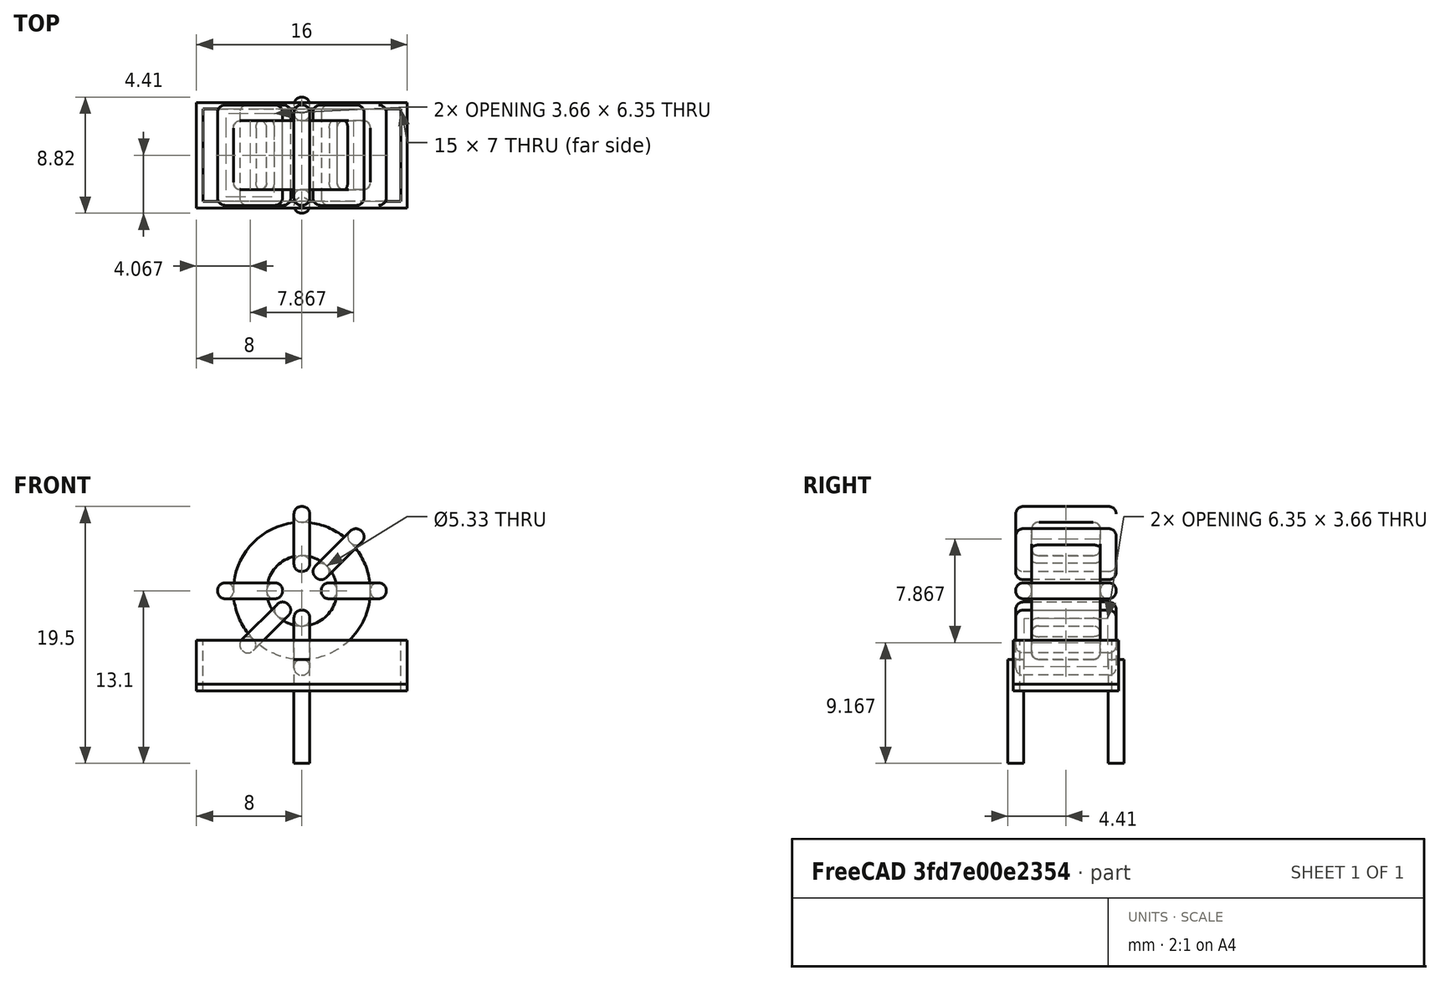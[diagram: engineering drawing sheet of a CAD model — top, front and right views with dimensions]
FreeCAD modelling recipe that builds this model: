
FCSTD DOCUMENT  (FreeCAD 0.16R6703 (Git))
Label: L_Toroid_Vertical_L16.0mm_W8.0mm_P7.62mm
License: All rights reserved
LicenseURL: http://en.wikipedia.org/wiki/All_rights_reserved
objects: Sketcher::SketchObject×8, PartDesign::Pad×8, PartDesign::Fillet×5, Spreadsheet::Sheet×1
note: 29 computed .brp shape members not serialized (recipe doc carries the construction recipe); baked Part::Feature solids carry a one-line shape summary decoded from their .brp

FEATURE [Spreadsheet::Sheet] Spreadsheet  label="dimensions"
  cells = A1=Wx; B1(Wx)=12.8; C1(WW)=5.333333333333333; D1(iWx)=16; A2=Wy; B2(Wy)=7.62; D2(iWy)=8; A3=RM; B3(RMx)=7.62; C3(RMy)=0; A4=d_wire; B4(d_wire)=1.2; A5=H; B5(H)=16; A6=offsetx; B6(offsetx)=8
FEATURE [Sketcher::SketchObject] Sketch
  Placement = pos=(0,-3.81,0) rot=(1,0,0;1.5708rad)
  expr: Placement.Base.y = -Spreadsheet.RMx / 2
  expr: Constraints[0] = Spreadsheet.Wx / 2 - Spreadsheet.d_wire
  expr: Constraints[4] = Spreadsheet.WW / 2
  expr: Constraints[2] = Spreadsheet.Wx / 2 + Spreadsheet.d_wire + 0.5
  sketch-geometry (2):
    g0: Circle CenterX=0 CenterY=8.1 CenterZ=0 NormalX=0 NormalY=0 NormalZ=1 Radius=5.2
    g1: Circle CenterX=0 CenterY=8.1 CenterZ=0 NormalX=0 NormalY=0 NormalZ=1 Radius=2.66667
  constraints (5):
    c: Radius(g0) = 5.2
    c: DistanceX(g-1,g0) = 0
    c: DistanceY(g-1,g0) = 8.1
    c: Coincident(g1,g0)
    c: Radius(g1) = 2.66667
FEATURE [PartDesign::Pad] Pad
  Length = 5.22
  Length2 = 100
  Midplane = true
  Placement = pos=(0,-3.81,0) rot=(1,0,0;1.5708rad)
  Sketch = -> Sketch
  Type = 0
  expr: Length = Spreadsheet.Wy - 2 * Spreadsheet.d_wire
FEATURE [Sketcher::SketchObject] Sketch001
  Placement = pos=(0,0,1.7) rot=(0,0,1;0rad)
  expr: Placement.Base.z = 0.5 + Spreadsheet.d_wire
  expr: Constraints[4] = Spreadsheet.RMy
  expr: Constraints[2] = -Spreadsheet.RMx
  expr: Constraints[1] = Spreadsheet.d_wire / 2
  sketch-geometry (2):
    g0: Circle CenterX=0 CenterY=0 CenterZ=0 NormalX=0 NormalY=0 NormalZ=1 Radius=0.6
    g1: Circle CenterX=0 CenterY=-7.62 CenterZ=0 NormalX=0 NormalY=0 NormalZ=1 Radius=0.6
  constraints (5):
    c: Equal(g0,g1)
    c: Radius(g0) = 0.6
    c: DistanceY(g-1,g1) = -7.62
    c: Coincident(g0,g-1)
    c: DistanceX(g-1,g1) = 0
FEATURE [PartDesign::Pad] Pad001
  Length = 1.2
  Length2 = 6.7
  Placement = pos=(0,0,1.7) rot=(0,0,1;0rad)
  Reversed = true
  Sketch = -> Sketch001
  Type = 4
  expr: Length2 = 5.5 + Spreadsheet.d_wire
  expr: Length = Spreadsheet.d_wire
FEATURE [PartDesign::Fillet] Fillet
  Base = -> Pad [Edge6,Edge3,Edge2]
  Placement = pos=(0,-3.81,0) rot=(1,0,0;1.5708rad)
  Radius = 0.5
FEATURE [Sketcher::SketchObject] Sketch003
  Placement = pos=(0,0,8.1) rot=(1,0,0;3.14159rad)
  expr: Constraints[18] = Spreadsheet.d_wire
  expr: Constraints[16] = Spreadsheet.d_wire
  expr: Constraints[19] = Spreadsheet.d_wire
  expr: Constraints[17] = Spreadsheet.d_wire
  expr: Placement.Base.y = -1 * (Spreadsheet.RMx - Spreadsheet.Wy) / 2
  expr: Constraints[21] = (Spreadsheet.Wx - Spreadsheet.WW) / 2 - Spreadsheet.d_wire
  expr: Constraints[22] = Spreadsheet.Wx / 2 - Spreadsheet.d_wire
  expr: Constraints[43] = Spreadsheet.d_wire
  expr: Constraints[48] = Spreadsheet.Wx - Spreadsheet.d_wire * 2
  expr: Constraints[49] = Spreadsheet.Wy
  expr: Placement.Base.z = Spreadsheet.Wx / 2 + Spreadsheet.d_wire + 0.5
  sketch-geometry (16):
    g0: LineSegment StartX=-1.46667 StartY=0 StartZ=0 EndX=-6.4 EndY=0 EndZ=0
    g1: LineSegment StartX=-6.4 StartY=0 StartZ=0 EndX=-6.4 EndY=7.62 EndZ=0
    g2: LineSegment StartX=-6.4 StartY=7.62 StartZ=0 EndX=-1.46667 EndY=7.62 EndZ=0
    g3: LineSegment StartX=-1.46667 StartY=7.62 StartZ=0 EndX=-1.46667 EndY=0 EndZ=0
    g4: LineSegment StartX=-5.2 StartY=6.42 StartZ=0 EndX=-2.66667 EndY=6.42 EndZ=0
    g5: LineSegment StartX=-2.66667 StartY=6.42 StartZ=0 EndX=-2.66667 EndY=1.2 EndZ=0
    g6: LineSegment StartX=-2.66667 StartY=1.2 StartZ=0 EndX=-5.2 EndY=1.2 EndZ=0
    g7: LineSegment StartX=-5.2 StartY=1.2 StartZ=0 EndX=-5.2 EndY=6.42 EndZ=0
    g8: LineSegment StartX=1.46667 StartY=7.62 StartZ=0 EndX=6.4 EndY=7.62 EndZ=0
    g9: LineSegment StartX=6.4 StartY=7.62 StartZ=0 EndX=6.4 EndY=0 EndZ=0
    g10: LineSegment StartX=6.4 StartY=0 StartZ=0 EndX=1.46667 EndY=0 EndZ=0
    g11: LineSegment StartX=1.46667 StartY=0 StartZ=0 EndX=1.46667 EndY=7.62 EndZ=0
    g12: LineSegment StartX=2.66667 StartY=6.42 StartZ=0 EndX=5.2 EndY=6.42 EndZ=0
    g13: LineSegment StartX=5.2 StartY=6.42 StartZ=0 EndX=5.2 EndY=1.2 EndZ=0
    g14: LineSegment StartX=5.2 StartY=1.2 StartZ=0 EndX=2.66667 EndY=1.2 EndZ=0
    g15: LineSegment StartX=2.66667 StartY=1.2 StartZ=0 EndX=2.66667 EndY=6.42 EndZ=0
  constraints (50):
    c: Horizontal(g0)
    c: Coincident(g1,g0)
    c: Vertical(g1)
    c: Coincident(g2,g1)
    c: Horizontal(g2)
    c: Coincident(g3,g2)
    c: Coincident(g3,g0)
    c: Vertical(g3)
    c: Coincident(g4,g5)
    c: Coincident(g5,g6)
    c: Coincident(g6,g7)
    c: Coincident(g7,g4)
    c: Horizontal(g4)
    c: Horizontal(g6)
    c: Vertical(g5)
    c: Vertical(g7)
    c: DistanceX(g1,g4) = 1.2
    c: DistanceY(g4,g1) = 1.2
    c: DistanceX(g5,g0) = 1.2
    c: DistanceY(g0,g5) = 1.2
    c: DistanceY(g-1,g0) = 0
    c: DistanceX(g6,g6) = 2.53333
    c: DistanceX(g6,g-1) = 5.2
    c: Coincident(g8,g9)
    c: Coincident(g9,g10)
    c: Coincident(g10,g11)
    c: Coincident(g11,g8)
    c: Horizontal(g8)
    c: Horizontal(g10)
    c: Vertical(g9)
    c: Vertical(g11)
    c: Coincident(g12,g13)
    c: Coincident(g13,g14)
    c: Coincident(g14,g15)
    c: Coincident(g15,g12)
    c: Horizontal(g12)
    c: Horizontal(g14)
    c: Vertical(g13)
    c: Vertical(g15)
    c: DistanceY(g8,g2) = 0
    c: DistanceY(g10,g0) = 0
    c: DistanceY(g14,g5) = 0
    c: DistanceY(g12,g4) = 0
    c: DistanceX(g8,g12) = 1.2
    c: Equal(g8,g2)
    c: Equal(g12,g4)
    c: Equal(g9,g1)
    c: Equal(g13,g7)
    c: DistanceX(g4,g12) = 10.4
    c: DistanceY(g0,g1) = 7.62
FEATURE [PartDesign::Pad] Pad002
  Length = 1.2
  Length2 = 100
  Midplane = true
  Placement = pos=(0,0,8.1) rot=(1,0,0;3.14159rad)
  Sketch = -> Sketch003
  Type = 0
  expr: Length = Spreadsheet.d_wire
FEATURE [PartDesign::Fillet] Fillet001
  Base = -> Pad002 [Edge38,Edge41,Edge42,Edge43,Edge29,Edge32,Edge33,Edge34,Edge25,Edge35,Edge36,Edge13,Edge14,Edge15,Edge16,Edge17,Edge18,Edge19,Edge1,Edge2,Edge3,Edge4,Edge5,Edge6,Edge7,Edge37,Edge39,Edge40,Edge20,Edge23,Edge24,Edge21,Edge22,Edge8,Edge9,Edge10,Edge11,Edge12,Edge26,Edge27,+8 more]
  Placement = pos=(0,0,8.1) rot=(1,0,0;3.14159rad)
  Radius = 0.564
  expr: Radius = Spreadsheet.d_wire * 0.47
FEATURE [Sketcher::SketchObject] Sketch004
  Placement = pos=(0,0,8.1) rot=(0.92388,0,0.382683;3.14159rad)
  expr: Constraints[18] = Spreadsheet.d_wire
  expr: Constraints[16] = Spreadsheet.d_wire
  expr: Constraints[19] = Spreadsheet.d_wire
  expr: Constraints[17] = Spreadsheet.d_wire
  expr: Placement.Base.y = -1 * (Spreadsheet.RMx - Spreadsheet.Wy) / 2
  expr: Constraints[21] = (Spreadsheet.Wx - Spreadsheet.WW) / 2 - Spreadsheet.d_wire
  expr: Constraints[22] = Spreadsheet.Wx / 2 - Spreadsheet.d_wire
  expr: Constraints[43] = Spreadsheet.d_wire
  expr: Constraints[48] = Spreadsheet.Wx - 2 * Spreadsheet.d_wire
  expr: Constraints[49] = Spreadsheet.Wy
  expr: Placement.Base.z = Spreadsheet.Wx / 2 + Spreadsheet.d_wire + 0.5
  sketch-geometry (16):
    g0: LineSegment StartX=-1.46667 StartY=0 StartZ=0 EndX=-6.4 EndY=0 EndZ=0
    g1: LineSegment StartX=-6.4 StartY=0 StartZ=0 EndX=-6.4 EndY=7.62 EndZ=0
    g2: LineSegment StartX=-6.4 StartY=7.62 StartZ=0 EndX=-1.46667 EndY=7.62 EndZ=0
    g3: LineSegment StartX=-1.46667 StartY=7.62 StartZ=0 EndX=-1.46667 EndY=0 EndZ=0
    g4: LineSegment StartX=-5.2 StartY=6.42 StartZ=0 EndX=-2.66667 EndY=6.42 EndZ=0
    g5: LineSegment StartX=-2.66667 StartY=6.42 StartZ=0 EndX=-2.66667 EndY=1.2 EndZ=0
    g6: LineSegment StartX=-2.66667 StartY=1.2 StartZ=0 EndX=-5.2 EndY=1.2 EndZ=0
    g7: LineSegment StartX=-5.2 StartY=1.2 StartZ=0 EndX=-5.2 EndY=6.42 EndZ=0
    g8: LineSegment StartX=1.46667 StartY=7.62 StartZ=0 EndX=6.4 EndY=7.62 EndZ=0
    g9: LineSegment StartX=6.4 StartY=7.62 StartZ=0 EndX=6.4 EndY=0 EndZ=0
    g10: LineSegment StartX=6.4 StartY=0 StartZ=0 EndX=1.46667 EndY=0 EndZ=0
    g11: LineSegment StartX=1.46667 StartY=0 StartZ=0 EndX=1.46667 EndY=7.62 EndZ=0
    g12: LineSegment StartX=2.66667 StartY=6.42 StartZ=0 EndX=5.2 EndY=6.42 EndZ=0
    g13: LineSegment StartX=5.2 StartY=6.42 StartZ=0 EndX=5.2 EndY=1.2 EndZ=0
    g14: LineSegment StartX=5.2 StartY=1.2 StartZ=0 EndX=2.66667 EndY=1.2 EndZ=0
    g15: LineSegment StartX=2.66667 StartY=1.2 StartZ=0 EndX=2.66667 EndY=6.42 EndZ=0
  constraints (50):
    c: Horizontal(g0)
    c: Coincident(g1,g0)
    c: Vertical(g1)
    c: Coincident(g2,g1)
    c: Horizontal(g2)
    c: Coincident(g3,g2)
    c: Coincident(g3,g0)
    c: Vertical(g3)
    c: Coincident(g4,g5)
    c: Coincident(g5,g6)
    c: Coincident(g6,g7)
    c: Coincident(g7,g4)
    c: Horizontal(g4)
    c: Horizontal(g6)
    c: Vertical(g5)
    c: Vertical(g7)
    c: DistanceX(g1,g4) = 1.2
    c: DistanceY(g4,g1) = 1.2
    c: DistanceX(g5,g0) = 1.2
    c: DistanceY(g0,g5) = 1.2
    c: DistanceY(g-1,g0) = 0
    c: DistanceX(g6,g6) = 2.53333
    c: DistanceX(g6,g-1) = 5.2
    c: Coincident(g8,g9)
    c: Coincident(g9,g10)
    c: Coincident(g10,g11)
    c: Coincident(g11,g8)
    c: Horizontal(g8)
    c: Horizontal(g10)
    c: Vertical(g9)
    c: Vertical(g11)
    c: Coincident(g12,g13)
    c: Coincident(g13,g14)
    c: Coincident(g14,g15)
    c: Coincident(g15,g12)
    c: Horizontal(g12)
    c: Horizontal(g14)
    c: Vertical(g13)
    c: Vertical(g15)
    c: DistanceY(g8,g2) = 0
    c: DistanceY(g10,g0) = 0
    c: DistanceY(g14,g5) = 0
    c: DistanceY(g12,g4) = 0
    c: DistanceX(g8,g12) = 1.2
    c: Equal(g8,g2)
    c: Equal(g12,g4)
    c: Equal(g9,g1)
    c: Equal(g13,g7)
    c: DistanceX(g4,g12) = 10.4
    c: DistanceY(g0,g1) = 7.62
FEATURE [PartDesign::Pad] Pad003
  Length = 1.2
  Length2 = 100
  Midplane = true
  Placement = pos=(0,0,8.1) rot=(0.92388,0,0.382683;3.14159rad)
  Sketch = -> Sketch004
  Type = 0
  expr: Length = Spreadsheet.d_wire
FEATURE [PartDesign::Fillet] Fillet002
  Base = -> Pad003 [Edge38,Edge41,Edge42,Edge43,Edge29,Edge32,Edge33,Edge34,Edge25,Edge35,Edge36,Edge13,Edge14,Edge15,Edge16,Edge17,Edge18,Edge19,Edge1,Edge2,Edge3,Edge4,Edge5,Edge6,Edge7,Edge37,Edge39,Edge40,Edge20,Edge23,Edge24,Edge21,Edge22,Edge8,Edge9,Edge10,Edge11,Edge12,Edge26,Edge27,+8 more]
  Placement = pos=(0,0,8.1) rot=(0.92388,0,0.382683;3.14159rad)
  Radius = 0.564
  expr: Radius = Spreadsheet.d_wire * 0.47
FEATURE [Sketcher::SketchObject] Sketch005
  Placement = pos=(0,0,8.1) rot=(0.92388,0,-0.382683;3.14159rad)
  expr: Constraints[18] = Spreadsheet.d_wire
  expr: Constraints[16] = Spreadsheet.d_wire
  expr: Constraints[19] = Spreadsheet.d_wire
  expr: Constraints[17] = Spreadsheet.d_wire
  expr: Placement.Base.y = -1 * (Spreadsheet.RMx - Spreadsheet.Wy) / 2
  expr: Constraints[21] = (Spreadsheet.Wx - Spreadsheet.WW) / 2 - Spreadsheet.d_wire
  expr: Constraints[22] = Spreadsheet.Wx / 2 - Spreadsheet.d_wire
  expr: Constraints[43] = Spreadsheet.d_wire
  expr: Constraints[48] = Spreadsheet.Wx - 2 * Spreadsheet.d_wire
  expr: Constraints[49] = Spreadsheet.Wy
  expr: Placement.Base.z = Spreadsheet.Wx / 2 + Spreadsheet.d_wire + 0.5
  sketch-geometry (16):
    g0: LineSegment StartX=-1.46667 StartY=0 StartZ=0 EndX=-6.4 EndY=0 EndZ=0
    g1: LineSegment StartX=-6.4 StartY=0 StartZ=0 EndX=-6.4 EndY=7.62 EndZ=0
    g2: LineSegment StartX=-6.4 StartY=7.62 StartZ=0 EndX=-1.46667 EndY=7.62 EndZ=0
    g3: LineSegment StartX=-1.46667 StartY=7.62 StartZ=0 EndX=-1.46667 EndY=0 EndZ=0
    g4: LineSegment StartX=-5.2 StartY=6.42 StartZ=0 EndX=-2.66667 EndY=6.42 EndZ=0
    g5: LineSegment StartX=-2.66667 StartY=6.42 StartZ=0 EndX=-2.66667 EndY=1.2 EndZ=0
    g6: LineSegment StartX=-2.66667 StartY=1.2 StartZ=0 EndX=-5.2 EndY=1.2 EndZ=0
    g7: LineSegment StartX=-5.2 StartY=1.2 StartZ=0 EndX=-5.2 EndY=6.42 EndZ=0
    g8: LineSegment StartX=1.46667 StartY=7.62 StartZ=0 EndX=6.4 EndY=7.62 EndZ=0
    g9: LineSegment StartX=6.4 StartY=7.62 StartZ=0 EndX=6.4 EndY=0 EndZ=0
    g10: LineSegment StartX=6.4 StartY=0 StartZ=0 EndX=1.46667 EndY=0 EndZ=0
    g11: LineSegment StartX=1.46667 StartY=0 StartZ=0 EndX=1.46667 EndY=7.62 EndZ=0
    g12: LineSegment StartX=2.66667 StartY=6.42 StartZ=0 EndX=5.2 EndY=6.42 EndZ=0
    g13: LineSegment StartX=5.2 StartY=6.42 StartZ=0 EndX=5.2 EndY=1.2 EndZ=0
    g14: LineSegment StartX=5.2 StartY=1.2 StartZ=0 EndX=2.66667 EndY=1.2 EndZ=0
    g15: LineSegment StartX=2.66667 StartY=1.2 StartZ=0 EndX=2.66667 EndY=6.42 EndZ=0
  constraints (50):
    c: Horizontal(g0)
    c: Coincident(g1,g0)
    c: Vertical(g1)
    c: Coincident(g2,g1)
    c: Horizontal(g2)
    c: Coincident(g3,g2)
    c: Coincident(g3,g0)
    c: Vertical(g3)
    c: Coincident(g4,g5)
    c: Coincident(g5,g6)
    c: Coincident(g6,g7)
    c: Coincident(g7,g4)
    c: Horizontal(g4)
    c: Horizontal(g6)
    c: Vertical(g5)
    c: Vertical(g7)
    c: DistanceX(g1,g4) = 1.2
    c: DistanceY(g4,g1) = 1.2
    c: DistanceX(g5,g0) = 1.2
    c: DistanceY(g0,g5) = 1.2
    c: DistanceY(g-1,g0) = 0
    c: DistanceX(g6,g6) = 2.53333
    c: DistanceX(g6,g-1) = 5.2
    c: Coincident(g8,g9)
    c: Coincident(g9,g10)
    c: Coincident(g10,g11)
    c: Coincident(g11,g8)
    c: Horizontal(g8)
    c: Horizontal(g10)
    c: Vertical(g9)
    c: Vertical(g11)
    c: Coincident(g12,g13)
    c: Coincident(g13,g14)
    c: Coincident(g14,g15)
    c: Coincident(g15,g12)
    c: Horizontal(g12)
    c: Horizontal(g14)
    c: Vertical(g13)
    c: Vertical(g15)
    c: DistanceY(g8,g2) = 0
    c: DistanceY(g10,g0) = 0
    c: DistanceY(g14,g5) = 0
    c: DistanceY(g12,g4) = 0
    c: DistanceX(g8,g12) = 1.2
    c: Equal(g8,g2)
    c: Equal(g12,g4)
    c: Equal(g9,g1)
    c: Equal(g13,g7)
    c: DistanceX(g4,g12) = 10.4
    c: DistanceY(g0,g1) = 7.62
FEATURE [PartDesign::Pad] Pad004
  Length = 1.2
  Length2 = 100
  Midplane = true
  Placement = pos=(0,0,8.1) rot=(0.92388,0,-0.382683;3.14159rad)
  Sketch = -> Sketch005
  Type = 0
  expr: Length = Spreadsheet.d_wire
FEATURE [PartDesign::Fillet] Fillet003
  Base = -> Pad004 [Edge38,Edge41,Edge42,Edge43,Edge29,Edge32,Edge33,Edge34,Edge25,Edge35,Edge36,Edge13,Edge14,Edge15,Edge16,Edge17,Edge18,Edge19,Edge1,Edge2,Edge3,Edge4,Edge5,Edge6,Edge7,Edge37,Edge39,Edge40,Edge20,Edge23,Edge24,Edge21,Edge22,Edge8,Edge9,Edge10,Edge11,Edge12,Edge26,Edge27,+8 more]
  Placement = pos=(0,0,8.1) rot=(0.92388,0,-0.382683;3.14159rad)
  Radius = 0.564
  expr: Radius = Spreadsheet.d_wire * 0.47
FEATURE [Sketcher::SketchObject] Sketch006
  Placement = pos=(0,0,8.1) rot=(0.707107,0,0.707107;3.14159rad)
  expr: Constraints[18] = Spreadsheet.d_wire
  expr: Constraints[16] = Spreadsheet.d_wire
  expr: Constraints[19] = Spreadsheet.d_wire
  expr: Constraints[17] = Spreadsheet.d_wire
  expr: Placement.Base.y = -1 * (Spreadsheet.RMx - Spreadsheet.Wy) / 2
  expr: Constraints[21] = (Spreadsheet.Wx - Spreadsheet.WW) / 2 - Spreadsheet.d_wire
  expr: Constraints[22] = Spreadsheet.Wx / 2 - Spreadsheet.d_wire
  expr: Constraints[43] = Spreadsheet.d_wire
  expr: Constraints[48] = Spreadsheet.Wx - Spreadsheet.d_wire * 2
  expr: Constraints[49] = Spreadsheet.Wy
  expr: Placement.Base.z = Spreadsheet.Wx / 2 + Spreadsheet.d_wire + 0.5
  sketch-geometry (16):
    g0: LineSegment StartX=-1.46667 StartY=0 StartZ=0 EndX=-6.4 EndY=0 EndZ=0
    g1: LineSegment StartX=-6.4 StartY=0 StartZ=0 EndX=-6.4 EndY=7.62 EndZ=0
    g2: LineSegment StartX=-6.4 StartY=7.62 StartZ=0 EndX=-1.46667 EndY=7.62 EndZ=0
    g3: LineSegment StartX=-1.46667 StartY=7.62 StartZ=0 EndX=-1.46667 EndY=0 EndZ=0
    g4: LineSegment StartX=-5.2 StartY=6.42 StartZ=0 EndX=-2.66667 EndY=6.42 EndZ=0
    g5: LineSegment StartX=-2.66667 StartY=6.42 StartZ=0 EndX=-2.66667 EndY=1.2 EndZ=0
    g6: LineSegment StartX=-2.66667 StartY=1.2 StartZ=0 EndX=-5.2 EndY=1.2 EndZ=0
    g7: LineSegment StartX=-5.2 StartY=1.2 StartZ=0 EndX=-5.2 EndY=6.42 EndZ=0
    g8: LineSegment StartX=1.46667 StartY=7.62 StartZ=0 EndX=6.4 EndY=7.62 EndZ=0
    g9: LineSegment StartX=6.4 StartY=7.62 StartZ=0 EndX=6.4 EndY=0 EndZ=0
    g10: LineSegment StartX=6.4 StartY=0 StartZ=0 EndX=1.46667 EndY=0 EndZ=0
    g11: LineSegment StartX=1.46667 StartY=0 StartZ=0 EndX=1.46667 EndY=7.62 EndZ=0
    g12: LineSegment StartX=2.66667 StartY=6.42 StartZ=0 EndX=5.2 EndY=6.42 EndZ=0
    g13: LineSegment StartX=5.2 StartY=6.42 StartZ=0 EndX=5.2 EndY=1.2 EndZ=0
    g14: LineSegment StartX=5.2 StartY=1.2 StartZ=0 EndX=2.66667 EndY=1.2 EndZ=0
    g15: LineSegment StartX=2.66667 StartY=1.2 StartZ=0 EndX=2.66667 EndY=6.42 EndZ=0
  constraints (50):
    c: Horizontal(g0)
    c: Coincident(g1,g0)
    c: Vertical(g1)
    c: Coincident(g2,g1)
    c: Horizontal(g2)
    c: Coincident(g3,g2)
    c: Coincident(g3,g0)
    c: Vertical(g3)
    c: Coincident(g4,g5)
    c: Coincident(g5,g6)
    c: Coincident(g6,g7)
    c: Coincident(g7,g4)
    c: Horizontal(g4)
    c: Horizontal(g6)
    c: Vertical(g5)
    c: Vertical(g7)
    c: DistanceX(g1,g4) = 1.2
    c: DistanceY(g4,g1) = 1.2
    c: DistanceX(g5,g0) = 1.2
    c: DistanceY(g0,g5) = 1.2
    c: DistanceY(g-1,g0) = 0
    c: DistanceX(g6,g6) = 2.53333
    c: DistanceX(g6,g-1) = 5.2
    c: Coincident(g8,g9)
    c: Coincident(g9,g10)
    c: Coincident(g10,g11)
    c: Coincident(g11,g8)
    c: Horizontal(g8)
    c: Horizontal(g10)
    c: Vertical(g9)
    c: Vertical(g11)
    c: Coincident(g12,g13)
    c: Coincident(g13,g14)
    c: Coincident(g14,g15)
    c: Coincident(g15,g12)
    c: Horizontal(g12)
    c: Horizontal(g14)
    c: Vertical(g13)
    c: Vertical(g15)
    c: DistanceY(g8,g2) = 0
    c: DistanceY(g10,g0) = 0
    c: DistanceY(g14,g5) = 0
    c: DistanceY(g12,g4) = 0
    c: DistanceX(g8,g12) = 1.2
    c: Equal(g8,g2)
    c: Equal(g12,g4)
    c: Equal(g9,g1)
    c: Equal(g13,g7)
    c: DistanceX(g4,g12) = 10.4
    c: DistanceY(g0,g1) = 7.62
FEATURE [PartDesign::Pad] Pad005
  Length = 1.2
  Length2 = 100
  Midplane = true
  Placement = pos=(0,0,8.1) rot=(0.707107,0,0.707107;3.14159rad)
  Sketch = -> Sketch006
  Type = 0
  expr: Length = Spreadsheet.d_wire
FEATURE [PartDesign::Fillet] Fillet004
  Base = -> Pad005 [Edge38,Edge41,Edge42,Edge43,Edge29,Edge32,Edge33,Edge34,Edge25,Edge35,Edge36,Edge13,Edge14,Edge15,Edge16,Edge17,Edge18,Edge19,Edge1,Edge2,Edge3,Edge4,Edge5,Edge6,Edge7,Edge37,Edge39,Edge40,Edge20,Edge23,Edge24,Edge21,Edge22,Edge8,Edge9,Edge10,Edge11,Edge12,Edge26,Edge27,+8 more]
  Placement = pos=(0,0,8.1) rot=(0.707107,0,0.707107;3.14159rad)
  Radius = 0.564
  expr: Radius = Spreadsheet.d_wire * 0.47
FEATURE [Sketcher::SketchObject] Sketch007
  Placement = pos=(0,0,0.5) rot=(0,0,1;0rad)
  expr: Placement.Base.z = 0.5
  expr: Constraints[11] = Spreadsheet.iWx / 2
  expr: Constraints[10] = (Spreadsheet.iWy - Spreadsheet.RMx) / 2
  expr: Constraints[9] = Spreadsheet.iWy
  expr: Constraints[8] = Spreadsheet.iWx
  sketch-geometry (4):
    g0: LineSegment StartX=-8 StartY=0.19 StartZ=0 EndX=8 EndY=0.19 EndZ=0
    g1: LineSegment StartX=8 StartY=0.19 StartZ=0 EndX=8 EndY=-7.81 EndZ=0
    g2: LineSegment StartX=8 StartY=-7.81 StartZ=0 EndX=-8 EndY=-7.81 EndZ=0
    g3: LineSegment StartX=-8 StartY=-7.81 StartZ=0 EndX=-8 EndY=0.19 EndZ=0
  constraints (12):
    c: Coincident(g0,g1)
    c: Coincident(g1,g2)
    c: Coincident(g2,g3)
    c: Coincident(g3,g0)
    c: Horizontal(g0)
    c: Horizontal(g2)
    c: Vertical(g1)
    c: Vertical(g3)
    c: DistanceX(g0,g0) = 16
    c: DistanceY(g3,g3) = 8
    c: DistanceY(g-1,g0) = 0.19
    c: DistanceX(g0,g-1) = 8
FEATURE [PartDesign::Pad] Pad006
  Length = 0.5
  Length2 = 100
  Placement = pos=(0,0,0.5) rot=(0,0,1;0rad)
  Sketch = -> Sketch007
  Type = 0
FEATURE [Sketcher::SketchObject] Sketch008
  Placement = pos=(0,0,0.5) rot=(0,0,1;0rad)
  expr: Constraints[8] = Spreadsheet.iWx
  expr: Constraints[9] = Spreadsheet.iWy
  expr: Constraints[10] = (Spreadsheet.iWy - Spreadsheet.RMx) / 2
  expr: Placement.Base.z = 0.5
  expr: Constraints[21] = 0.5
  expr: Constraints[11] = Spreadsheet.iWx / 2
  sketch-geometry (8):
    g0: LineSegment StartX=-8 StartY=0.19 StartZ=0 EndX=8 EndY=0.19 EndZ=0
    g1: LineSegment StartX=8 StartY=0.19 StartZ=0 EndX=8 EndY=-7.81 EndZ=0
    g2: LineSegment StartX=8 StartY=-7.81 StartZ=0 EndX=-8 EndY=-7.81 EndZ=0
    g3: LineSegment StartX=-8 StartY=-7.81 StartZ=0 EndX=-8 EndY=0.19 EndZ=0
    g4: LineSegment StartX=-7.5 StartY=-0.31 StartZ=0 EndX=7.5 EndY=-0.31 EndZ=0
    g5: LineSegment StartX=7.5 StartY=-0.31 StartZ=0 EndX=7.5 EndY=-7.31 EndZ=0
    g6: LineSegment StartX=7.5 StartY=-7.31 StartZ=0 EndX=-7.5 EndY=-7.31 EndZ=0
    g7: LineSegment StartX=-7.5 StartY=-7.31 StartZ=0 EndX=-7.5 EndY=-0.31 EndZ=0
  constraints (24):
    c: Coincident(g0,g1)
    c: Coincident(g1,g2)
    c: Coincident(g2,g3)
    c: Coincident(g3,g0)
    c: Horizontal(g0)
    c: Horizontal(g2)
    c: Vertical(g1)
    c: Vertical(g3)
    c: DistanceX(g0,g0) = 16
    c: DistanceY(g3,g3) = 8
    c: DistanceY(g-1,g0) = 0.19
    c: DistanceX(g0,g-1) = 8
    c: Coincident(g4,g5)
    c: Coincident(g5,g6)
    c: Coincident(g6,g7)
    c: Coincident(g7,g4)
    c: Horizontal(g4)
    c: Horizontal(g6)
    c: Vertical(g5)
    c: Vertical(g7)
    c: DistanceX(g5,g1) = 0.5
    c: DistanceY(g1,g5) = 0.5
    c: DistanceX(g0,g4) = 0.5
    c: DistanceY(g4,g0) = 0.5
FEATURE [PartDesign::Pad] Pad007
  Length = 3.84
  Length2 = 100
  Placement = pos=(0,0,0.5) rot=(0,0,1;0rad)
  Sketch = -> Sketch008
  Type = 0
  expr: Length = Spreadsheet.Wx * 0.3
